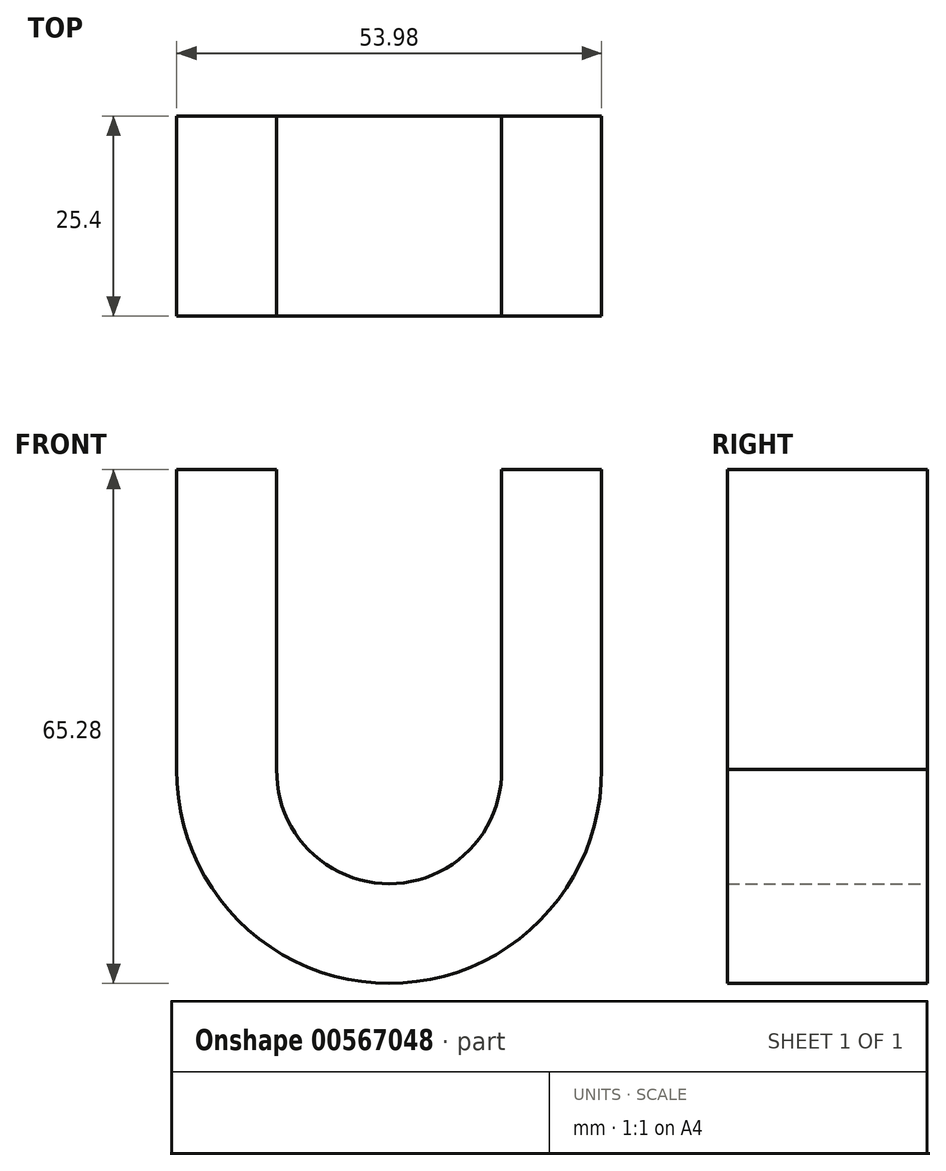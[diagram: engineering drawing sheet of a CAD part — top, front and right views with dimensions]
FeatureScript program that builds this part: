
annotation { "Feature Type Name" : "Feature", "Feature Type Description" : "" }
export const myFeature = defineFeature(function(context is Context, id is Id, definition is map)
    precondition{}
    {
        {
            var Q0;
            Q0=qCreatedBy(makeId("Front.planeOp"),FACE);
            var sketch = newSketch(context, id + "F0", { "sketchPlane" : qUnion([Q0])});
            skArc(sketch, "E0", {"start": v(-14.29, 0.23) * mm, "mid": v(0, -14.29) * mm, "end": v(14.29, 0.23) * mm});
            skLineSegment(sketch, "E1.bottom", {"start": v(14.29, 0.23) * mm, "end": v(14.29, 0.23) * mm});
            skLineSegment(sketch, "E1.left", {"start": v(-14.29, 0.23) * mm, "end": v(-14.29, 38.33) * mm});
            skLineSegment(sketch, "E1.right", {"start": v(14.29, 0.23) * mm, "end": v(14.29, 38.33) * mm});
            skLineSegment(sketch, "E2.top", {"start": v(-26.99, 38.33) * mm, "end": v(-14.29, 38.33) * mm});
            skLineSegment(sketch, "E2.left", {"start": v(-26.99, 0.23) * mm, "end": v(-26.99, 38.33) * mm});
            skLineSegment(sketch, "E2.right", {"start": v(26.99, 0.23) * mm, "end": v(26.99, 38.33) * mm});
            skArc(sketch, "E3.trimOffspring", {"start": v(-26.99, 0.23) * mm, "mid": v(0, -26.95) * mm, "end": v(26.99, 0.23) * mm});
            skLineSegment(sketch, "E4.trimOffspring", {"start": v(26.99, 0.23) * mm, "end": v(26.99, 0.23) * mm});
            skLineSegment(sketch, "E5.trimOffspring", {"start": v(14.29, 38.33) * mm, "end": v(26.99, 38.33) * mm});
            skSolve(sketch);
        }
        {
            var Q0;
            {var subQ4=sQuery(id+"F0.wireOp",EDGE,"E1.bottom");Q0=makeQuery(id+"F0.imprint","IMPRINT",FACE,{"disambiguationData":[TD([[makeQuery(id+"F0.imprint","IMPRINT",EDGE,{"derivedFrom":subQ4}),-1.0]])]});}
            var Q1;
            {var subQ4=sQuery(id+"F0.wireOp",EDGE,"E3.trimOffspring");Q1=makeQuery(id+"F0.imprint","IMPRINT",FACE,{"disambiguationData":[TD([[makeQuery(id+"F0.imprint","IMPRINT",EDGE,{"derivedFrom":subQ4}),1.0]])]});}
            var Q2;
            {var subQ0=sQuery(id+"F0.wireOp",EDGE,"E2.left");Q2=makeQuery(id+"F0.imprint","IMPRINT",FACE,{"disambiguationData":[TD([[makeQuery(id+"F0.imprint","IMPRINT",EDGE,{"derivedFrom":subQ0}),-1.0]])]});}
            extrude(context, id + "F1", {"entities" : qUnion([Q0, Q1, Q2]), "depth" : 25.4 * mm, "offsetDistance" : 25.4 * mm});
        }
    });
